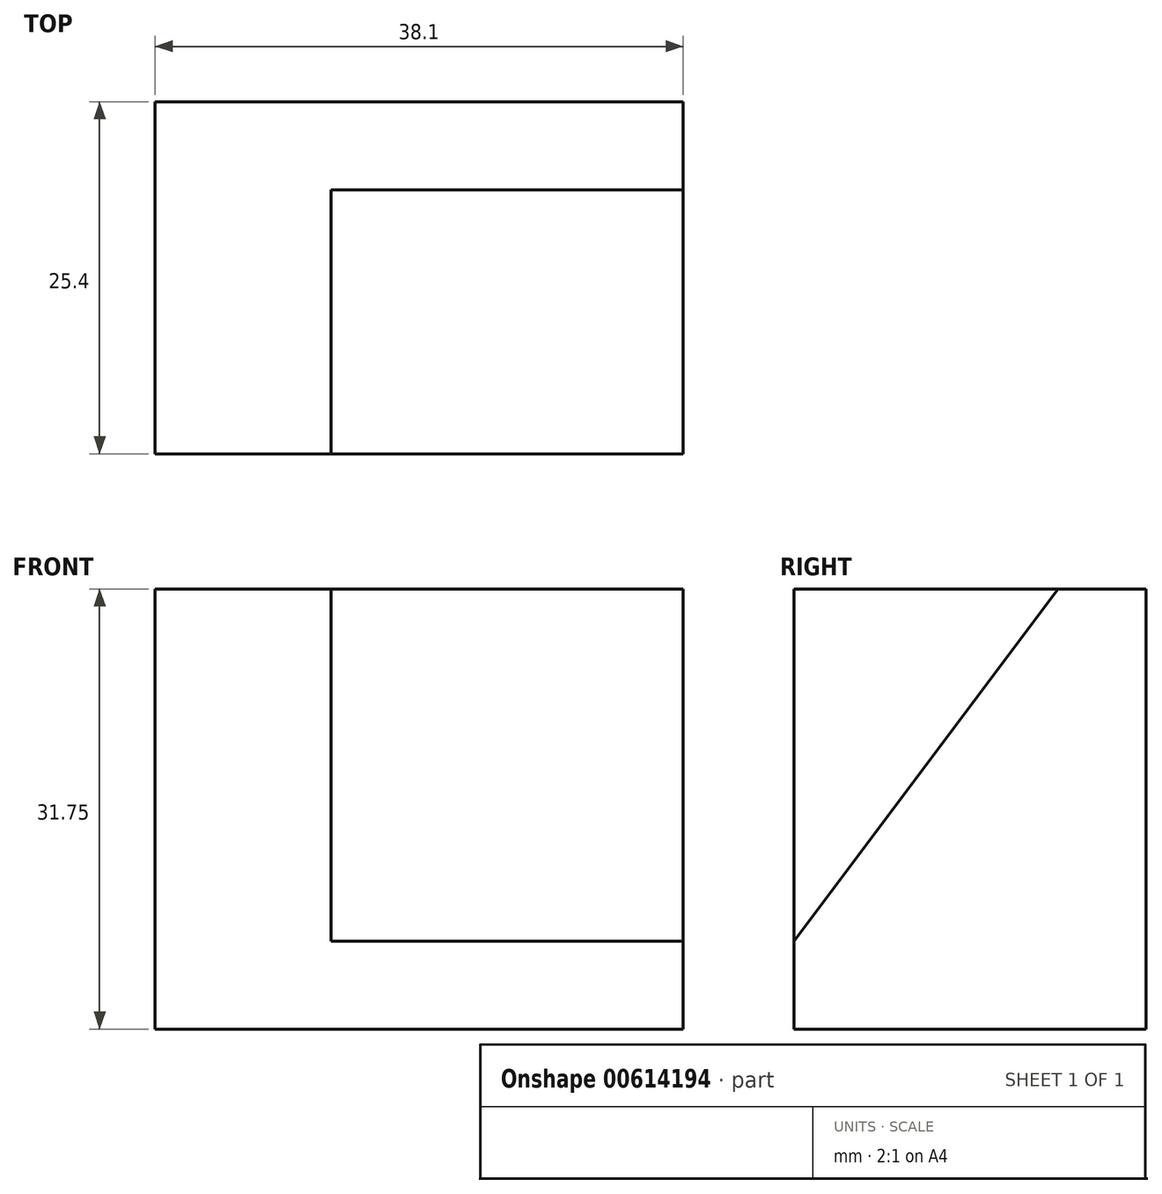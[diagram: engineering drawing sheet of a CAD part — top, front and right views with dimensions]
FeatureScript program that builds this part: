
annotation { "Feature Type Name" : "Feature", "Feature Type Description" : "" }
export const myFeature = defineFeature(function(context is Context, id is Id, definition is map)
    precondition{}
    {
        {
            var Q0;
            Q0=qCreatedBy(makeId("Front.planeOp"),FACE);
            var sketch = newSketch(context, id + "F0", { "sketchPlane" : qUnion([Q0])});
            skLineSegment(sketch, "E0", {"start": v(0, 0) * mm, "end": v(38.1, 0) * mm});
            skLineSegment(sketch, "E1", {"start": v(0, 0) * mm, "end": v(0, 31.75) * mm});
            skLineSegment(sketch, "E2", {"start": v(0, 31.75) * mm, "end": v(38.1, 31.75) * mm});
            skLineSegment(sketch, "E3", {"start": v(38.1, 31.75) * mm, "end": v(38.1, 0) * mm});
            skSolve(sketch);
        }
        {
            var Q0;
            Q0=makeQuery(id+"F0.imprint","IMPRINT",FACE,{"disambiguationData":[TD([[makeQuery(id+"F0.imprint","IMPRINT",EDGE,{"derivedFrom":sQuery(id+"F0.wireOp",EDGE,"E0")}),1.0]])]});
            extrude(context, id + "F1", {"entities" : qUnion([Q0]), "depth" : 25.4 * mm, "offsetDistance" : 25.4 * mm});
        }
        {
            var Q0;
            Q0=makeQuery(id+"F1.opExtrude","SWEPT_FACE",FACE,{"disambiguationData":[OSD([sQuery(id+"F0.wireOp",EDGE,"E3")])]});
            var sketch = newSketch(context, id + "F2", { "sketchPlane" : qUnion([Q0])});
            skLineSegment(sketch, "E4", {"start": v(0, 31.75) * mm, "end": v(-6.35, 31.75) * mm});
            skLineSegment(sketch, "E5", {"start": v(-25.4, 0) * mm, "end": v(-25.4, 6.35) * mm});
            skLineSegment(sketch, "E6", {"start": v(-6.35, 31.75) * mm, "end": v(-25.4, 6.35) * mm});
            skSolve(sketch);
        }
        {
            var Q0;
            Q0 = qSketchRegion(id + "F2", true);
            var Q1;
            {var subQ0=sQuery(id+"F2.wireOp",EDGE,"E6");Q1=makeQuery(id+"F2.imprint","IMPRINT",FACE,{"disambiguationData":[TD([[makeQuery(id+"F2.imprint","IMPRINT",EDGE,{"derivedFrom":subQ0}),-1.0]])]});}
            extrude(context, id + "F3", {"entities" : qUnion([Q0, Q1]), "operationType" : NewBodyOperationType.REMOVE, "oppositeDirection" : true, "depth" : 25.4 * mm, "offsetDistance" : 25.4 * mm});
        }
    });
